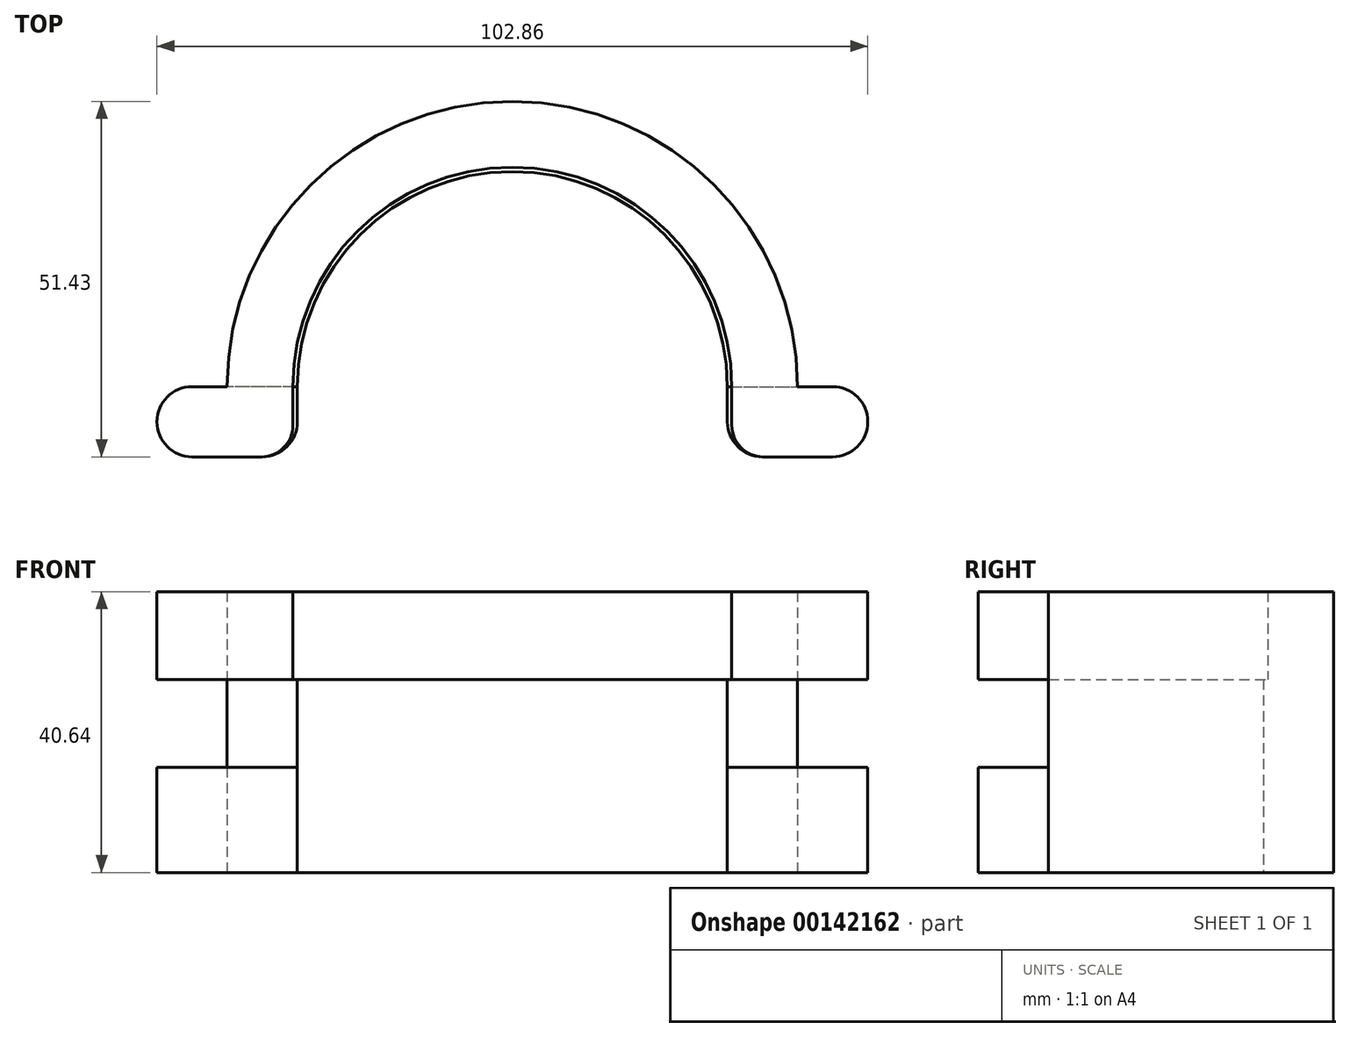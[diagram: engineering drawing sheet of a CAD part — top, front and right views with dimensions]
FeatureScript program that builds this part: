
annotation { "Feature Type Name" : "Feature", "Feature Type Description" : "" }
export const myFeature = defineFeature(function(context is Context, id is Id, definition is map)
    precondition{}
    {
        {
            var Q0;
            Q0=qCreatedBy(makeId("Top.planeOp"),FACE);
            var sketch = newSketch(context, id + "F0", { "sketchPlane" : qUnion([Q0])});
            skCircle(sketch, "E0", {"center": v(0, 0) * mm, "radius": 31.12 * mm});
            skCircle(sketch, "E1", {"center": v(0, 0) * mm, "radius": 41.28 * mm});
            skLineSegment(sketch, "E2", {"start": v(-31.12, 0) * mm, "end": v(-41.28, 0) * mm});
            skLineSegment(sketch, "E3", {"start": v(31.12, 0) * mm, "end": v(41.28, 0) * mm});
            skLineSegment(sketch, "E4.bottom", {"start": v(31.12, 0) * mm, "end": v(46.36, 0) * mm});
            skLineSegment(sketch, "E4.top", {"start": v(36.2, -10.16) * mm, "end": v(46.36, -10.16) * mm});
            skLineSegment(sketch, "E4.left", {"start": v(31.12, 0) * mm, "end": v(31.12, -5.08) * mm});
            skLineSegment(sketch, "E4.right", {"start": v(51.44, -5.08) * mm, "end": v(51.44, -5.08) * mm});
            skPoint(sketch, "E5.visualSharp", {"position": v(31.12, -10.16) * mm});
            skArc(sketch, "E5.filletArc", {"start": v(31.12, -5.08) * mm, "mid": v(32.6, -8.67) * mm, "end": v(36.2, -10.16) * mm});
            skPoint(sketch, "E6.visualSharp", {"position": v(51.44, -10.16) * mm});
            skArc(sketch, "E6.filletArc", {"start": v(46.36, -10.16) * mm, "mid": v(49.95, -8.67) * mm, "end": v(51.44, -5.08) * mm});
            skPoint(sketch, "E7.visualSharp", {"position": v(51.44, 0) * mm});
            skArc(sketch, "E7.filletArc", {"start": v(51.44, -5.08) * mm, "mid": v(49.95, -1.49) * mm, "end": v(46.36, 0) * mm});
            skLineSegment(sketch, "E8.bottom", {"start": v(-31.12, 0) * mm, "end": v(-46.36, 0) * mm});
            skLineSegment(sketch, "E8.top", {"start": v(-36.2, -10.16) * mm, "end": v(-46.36, -10.16) * mm});
            skLineSegment(sketch, "E8.left", {"start": v(-31.12, 0) * mm, "end": v(-31.12, -5.08) * mm});
            skLineSegment(sketch, "E8.right", {"start": v(-51.44, -5.08) * mm, "end": v(-51.44, -5.08) * mm});
            skPoint(sketch, "E9.visualSharp", {"position": v(-31.12, -10.16) * mm});
            skArc(sketch, "E9.filletArc", {"start": v(-36.2, -10.16) * mm, "mid": v(-32.6, -8.67) * mm, "end": v(-31.12, -5.08) * mm});
            skPoint(sketch, "E10.visualSharp", {"position": v(-51.44, -10.16) * mm});
            skArc(sketch, "E10.filletArc", {"start": v(-51.44, -5.08) * mm, "mid": v(-49.95, -8.67) * mm, "end": v(-46.36, -10.16) * mm});
            skPoint(sketch, "E11.visualSharp", {"position": v(-51.44, 0) * mm});
            skArc(sketch, "E11.filletArc", {"start": v(-46.36, 0) * mm, "mid": v(-49.95, -1.49) * mm, "end": v(-51.44, -5.08) * mm});
            skSolve(sketch);
        }
        {
            var Q0;
            {var subQ3=sQuery(id+"F0.wireOp",EDGE,"E8.bottom");var subQ5=sQuery(id+"F0.wireOp",EDGE,"E1");var subQ6=makeQuery(id+"F0.imprint","INTERSECT",VERTEX,{"derivedFrom":[subQ5,subQ3]});Q0=makeQuery(id+"F0.imprint","IMPRINT",FACE,{"disambiguationData":[TD([[makeQuery(id+"F0.imprint","IMPRINT",EDGE,{"disambiguationData":[TD([[subQ6,1.0]])],"derivedFrom":subQ5}),1.0]])]});}
            extrude(context, id + "F1", {"entities" : qUnion([Q0]), "depth" : 27.94 * mm});
        }
        {
            var Q0;
            {var subQ0=sQuery(id+"F0.wireOp",EDGE,"E10.filletArc");Q0=makeQuery(id+"F0.imprint","IMPRINT",FACE,{"disambiguationData":[TD([[makeQuery(id+"F0.imprint","IMPRINT",EDGE,{"derivedFrom":subQ0}),1.0]])]});}
            var Q1;
            {var subQ0=sQuery(id+"F0.wireOp",EDGE,"E8.left");Q1=makeQuery(id+"F0.imprint","IMPRINT",FACE,{"disambiguationData":[TD([[makeQuery(id+"F0.imprint","IMPRINT",EDGE,{"derivedFrom":subQ0}),-1.0]])]});}
            var Q2;
            {var subQ0=sQuery(id+"F0.wireOp",EDGE,"E4.left");Q2=makeQuery(id+"F0.imprint","IMPRINT",FACE,{"disambiguationData":[TD([[makeQuery(id+"F0.imprint","IMPRINT",EDGE,{"derivedFrom":subQ0}),1.0]])]});}
            var Q3;
            {var subQ0=sQuery(id+"F0.wireOp",EDGE,"E6.filletArc");Q3=makeQuery(id+"F0.imprint","IMPRINT",FACE,{"disambiguationData":[TD([[makeQuery(id+"F0.imprint","IMPRINT",EDGE,{"derivedFrom":subQ0}),1.0]])]});}
            extrude(context, id + "F2", {"entities" : qUnion([Q0, Q1, Q2, Q3]), "operationType" : NewBodyOperationType.ADD, "depth" : 15.24 * mm});
        }
        {
            var Q0;
            Q0=makeQuery(id+"F1.opExtrude","CAP_FACE",FACE,{"disambiguationData":[OSD([sQuery(id+"F0.wireOp",EDGE,"E0"),sQuery(id+"F0.wireOp",EDGE,"E1"),sQuery(id+"F0.wireOp",EDGE,"E4.bottom"),sQuery(id+"F0.wireOp",EDGE,"E8.bottom")])],"isStart":false});
            var sketch = newSketch(context, id + "F3", { "sketchPlane" : qUnion([Q0])});
            skCircle(sketch, "E12", {"center": v(0, 0) * mm, "radius": 31.75 * mm});
            skCircle(sketch, "E13", {"center": v(0, 0) * mm, "radius": 41.28 * mm});
            skLineSegment(sketch, "E14", {"start": v(-41.28, 0) * mm, "end": v(-31.75, 0) * mm});
            skLineSegment(sketch, "E15", {"start": v(41.28, 0) * mm, "end": v(31.75, 0) * mm});
            skLineSegment(sketch, "E16.bottom", {"start": v(31.75, 0) * mm, "end": v(46.35, 0) * mm});
            skLineSegment(sketch, "E16.top", {"start": v(36.32, -10.16) * mm, "end": v(46.35, -10.16) * mm});
            skLineSegment(sketch, "E16.left", {"start": v(31.75, 0) * mm, "end": v(31.75, -5.59) * mm});
            skLineSegment(sketch, "E16.right", {"start": v(51.44, -5.08) * mm, "end": v(51.44, -5.08) * mm});
            skLineSegment(sketch, "E17.bottom", {"start": v(-31.75, 0) * mm, "end": v(-46.35, 0) * mm});
            skLineSegment(sketch, "E17.top", {"start": v(-36.32, -10.16) * mm, "end": v(-46.35, -10.16) * mm});
            skLineSegment(sketch, "E17.left", {"start": v(-31.75, 0) * mm, "end": v(-31.75, -5.59) * mm});
            skLineSegment(sketch, "E17.right", {"start": v(-51.44, -5.08) * mm, "end": v(-51.44, -5.08) * mm});
            skPoint(sketch, "E18.visualSharp", {"position": v(-51.44, 0) * mm});
            skArc(sketch, "E18.filletArc", {"start": v(-46.35, 0) * mm, "mid": v(-49.95, -1.49) * mm, "end": v(-51.43, -5.08) * mm});
            skPoint(sketch, "E19.visualSharp", {"position": v(-51.44, -10.16) * mm});
            skArc(sketch, "E19.filletArc", {"start": v(-51.44, -5.08) * mm, "mid": v(-49.95, -8.67) * mm, "end": v(-46.35, -10.16) * mm});
            skPoint(sketch, "E20.visualSharp", {"position": v(51.44, 0) * mm});
            skArc(sketch, "E20.filletArc", {"start": v(51.44, -5.08) * mm, "mid": v(49.95, -1.49) * mm, "end": v(46.35, 0) * mm});
            skPoint(sketch, "E21.visualSharp", {"position": v(51.44, -10.16) * mm});
            skArc(sketch, "E21.filletArc", {"start": v(46.35, -10.16) * mm, "mid": v(49.95, -8.67) * mm, "end": v(51.44, -5.08) * mm});
            skPoint(sketch, "E22.visualSharp", {"position": v(31.75, -10.16) * mm});
            skArc(sketch, "E22.filletArc", {"start": v(31.75, -5.59) * mm, "mid": v(33.09, -8.82) * mm, "end": v(36.32, -10.16) * mm});
            skPoint(sketch, "E23.visualSharp", {"position": v(-31.75, -10.16) * mm});
            skArc(sketch, "E23.filletArc", {"start": v(-36.32, -10.16) * mm, "mid": v(-33.09, -8.82) * mm, "end": v(-31.75, -5.59) * mm});
            skSolve(sketch);
        }
        {
            var Q0;
            {var subQ0=sQuery(id+"F3.wireOp",EDGE,"E18.filletArc");Q0=makeQuery(id+"F3.imprint","IMPRINT",FACE,{"disambiguationData":[TD([[makeQuery(id+"F3.imprint","IMPRINT",EDGE,{"derivedFrom":subQ0}),1.0]])]});}
            var Q1;
            {var subQ0=sQuery(id+"F3.wireOp",EDGE,"E17.left");Q1=makeQuery(id+"F3.imprint","IMPRINT",FACE,{"disambiguationData":[TD([[makeQuery(id+"F3.imprint","IMPRINT",EDGE,{"derivedFrom":subQ0}),-1.0]])]});}
            var Q2;
            {var subQ3=sQuery(id+"F3.wireOp",EDGE,"E17.bottom");var subQ5=sQuery(id+"F3.wireOp",EDGE,"E13");var subQ6=makeQuery(id+"F3.imprint","INTERSECT",VERTEX,{"derivedFrom":[subQ5,subQ3]});Q2=makeQuery(id+"F3.imprint","IMPRINT",FACE,{"disambiguationData":[TD([[makeQuery(id+"F3.imprint","IMPRINT",EDGE,{"disambiguationData":[TD([[subQ6,1.0]])],"derivedFrom":subQ5}),1.0]])]});}
            var Q3;
            {var subQ0=sQuery(id+"F3.wireOp",EDGE,"E16.left");Q3=makeQuery(id+"F3.imprint","IMPRINT",FACE,{"disambiguationData":[TD([[makeQuery(id+"F3.imprint","IMPRINT",EDGE,{"derivedFrom":subQ0}),1.0]])]});}
            var Q4;
            {var subQ0=sQuery(id+"F3.wireOp",EDGE,"E20.filletArc");Q4=makeQuery(id+"F3.imprint","IMPRINT",FACE,{"disambiguationData":[TD([[makeQuery(id+"F3.imprint","IMPRINT",EDGE,{"derivedFrom":subQ0}),1.0]])]});}
            extrude(context, id + "F4", {"entities" : qUnion([Q0, Q1, Q2, Q3, Q4]), "operationType" : NewBodyOperationType.ADD, "depth" : 12.7 * mm});
        }
    });
